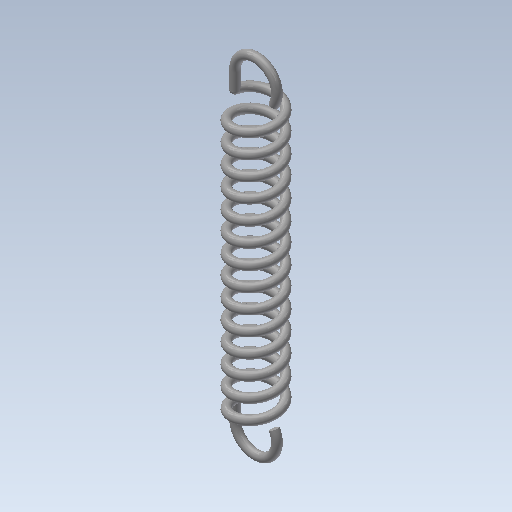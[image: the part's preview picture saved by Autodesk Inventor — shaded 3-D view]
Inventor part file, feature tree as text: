
AUTODESK INVENTOR PART (.ipt)
format: ipt  version: 2020.1 (Build 241239000, 239)  size: 1,151,488 bytes
history: native  units: mm
features: sketch x104, plane x32, other x32, extrude x10, sweep x6
ambient origin geometry x8: Origin, YZ Plane, XZ Plane, XY Plane, X Axis, Y Axis, Z Axis, Center Point
bodies: Solid1 (feature_tree)
feature tree (184):
  sketch  "Sketch1"  dims[d0=0.125mm d1=1.25mm]
  sketch  "3D Sketch2"
  plane  "Work PlaneSweep1"
  other  "First revolution with hook type 0(Right)"
  sketch  "Sketch8"  dims[d17=90.0deg d24=0.0mm d25=1.142857mm]
  plane  "Work PlaneExtrusion7"
  sketch  "Sketch10"  dims[d28=0.0mm d29=90.0deg d30=90.0deg d31=0.0mm d32=0.0mm d33=0.5mm]
  plane  "Work PlaneSweep2"
  sweep  "Sweep2"
  other  "Second revolution with hook type 0(Right)"
  sketch  "Sketch12"  dims[d38=90.0deg d54=10.0mm d55=10.0mm]
  plane  "Work PlaneExtrusion8"
  sketch  "Sketch110"  dims[d367=29.670597mm]
  sketch  "3D Sketch20"
  plane  "Work PlaneSweep3"
  sketch  "3D Sketch3"
  plane  "Work PlaneSweep6"
  other  "First revolution with hook type 0(Left)"
  sketch  "Sketch24"  dims[d180=90.0deg]
  plane  "Work PlaneExtrusion5"
  sketch  "Sketch18"  dims[d169=300.0deg d170=1.0mm]
  plane  "Work PlaneSweep7"
  sweep  "Sweep7"
  other  "Second revolution with hook type 0(Left)"
  sketch  "Sketch20"  dims[d173=300.0deg d174=1.0mm]
  plane  "Work PlaneExtrusion6"
  sketch  "Sketch22"  dims[d177=1.125mm d178=0.0mm]
  plane  "Work PlaneSweep8"
  other  "First revolution with hook type 1(Left)"
  sketch  "Sketch27"  dims[d182=1.125mm]
  plane  "Work PlaneExtrusion9"
  extrude  "Extrusion9"  TaperAngle=90.0deg  [1 undecoded]
  sketch  "Sketch29"  dims[d184=30.0mm d185=30.0mm d186=30.0mm]
  plane  "Work PlaneSweep9"
  other  "Second revolution with hook type 1(Left)"
  sketch  "Sketch32"  dims[d189=1.25mm]
  plane  "Work PlaneExtrusion10"
  sketch  "Sketch34"  dims[d191=300.0deg]
  sketch  "3D Sketch22"
  plane  "Work PlaneSweep10"
  other  "First revolution with hook type 1(Right)"
  sketch  "Sketch42"  dims[d195=40.0mm]
  plane  "Work PlaneExtrusion11"
  extrude  "Extrusion11"  Depth=1.142857mm TaperAngle=0.0deg
  sketch  "Sketch44"  dims[d197=0.0mm]
  plane  "Work PlaneSweep11"
  other  "Second revolution with hook type 1(Right)"
  sketch  "Sketch112"  dims[d373=20.0mm]
  plane  "Work PlaneExtrusion12"
  sketch  "Sketch114"  dims[d375=0.0mm]
  sketch  "3D Sketch24"
  plane  "Work PlaneSweep12"
  sketch  "Sketch46"  dims[d199=300.0deg]
  other  "First sweep with hook type 2(Left)"
  sweep  "SweepLeftHook21"
  sketch  "Sketch48"  dims[d200=1.0mm]
  other  "Second sweep with hook type 2(Left)"
  sweep  "SweepLeftHook22"
  sketch  "Sketch50"  dims[d201=0.0mm]
  other  "First sweep with hook type 2(Right)"
  sweep  "SweepRightHook21"
  sketch  "Sketch52"  dims[d202=90.0deg]
  other  "Second sweep with hook type 2(Right)"
  sweep  "SweepRightHook22"
  other  "First revolution with hook type 3(Left)"
  extrude  "Extrusion1"  Depth=20.0mm
  other  "Second revolution with hook type 3(Left)"
  extrude  "Extrusion2"  Depth=20.0mm
  sketch  "Sketch60"  dims[d209=90.0deg]
  plane  "Work PlaneSweep20"
  other  "First revolution with hook type 3(Right)"
  extrude  "Extrusion3"  Depth=20.0mm
  other  "Second revolution with hook type 3(Right)"
  extrude  "Extrusion4"  Depth=1.0mm
  sketch  "Sketch68"  dims[d216=40.0mm]
  plane  "Work Plane46"
  other  "First revolution with hook type 4(Left)"
  sketch  "Sketch71"  dims[d223=90.0deg]
  plane  "Work PlaneExtrusion13"
  extrude  "Extrusion13"  TaperAngle=90.0deg  [1 undecoded]
  sketch  "Sketch73"  dims[d229=90.0deg]
  plane  "Work PlaneSweep23"
  other  "Second revolution with hook type 4(Left)"
  sketch  "Sketch76"  dims[d238=50.0mm]
  plane  "Work PlaneExtrusion14"
  sketch  "Sketch78"  dims[d243=60.0mm]
  sketch  "3D Sketch26"
  plane  "Work PlaneSweep24"
  other  "First revolution with hook type 4(Right)"
  sketch  "Sketch86"  dims[d269=60.0mm]
  plane  "Work PlaneExtrusion15"
  extrude  "Extrusion15"  Depth=1.0mm
  sketch  "Sketch88"  dims[d282=60.0mm]
  plane  "Work PlaneSweep25"
  other  "Second revolution with hook type 4(Right)"
  sketch  "Sketch116"  dims[d377=210.0deg]
  plane  "Work PlaneExtrusion16"
  sketch  "Sketch118"  dims[d381=20.0mm]
  sketch  "3D Sketch28"
  plane  "Work PlaneSweep26"
  other  "First revolution with hook type 5(Left)"
  sketch  "Sketch91"  dims[d301=10.0mm d302=15.0mm d303=0.0mm d304=90.0deg d305=90.0deg d306=0.0mm d307=0.0mm]
  plane  "Work PlaneExtrusion17"
  extrude  "Extrusion17"  TaperAngle=300.0deg  [1 undecoded]
  other  "Second revolution with hook type 5(Left)"
  sketch  "Sketch95"  dims[d320=1.125mm]
  plane  "Work PlaneExtrusion18"
  other  "First revolution with hook type 5(Right)"
  sketch  "Sketch99"  dims[d331=1.0mm]
  plane  "Work PlaneExtrusion19"
  other  "Second revolution with hook type 5(Right)"
  sketch  "Sketch103"  dims[d364=1.0mm]
  plane  "Work PlaneExtrusion20"
  extrude  "Extrusion20"  TaperAngle=0.0deg  [1 undecoded]
  sketch  "Sketch105"  dims[d366=10.0mm]
  other  "First coil with hook type 6(Left)"
  other  "Second coil with hook type 6(Left)"
  other  "First coil with hook type 6(Right)"
  other  "Second coil with hook type 6(Right)"
  other  "Srf1"
  sketch  "Sketch3"  dims[d2=1.142857mm d3=10.0mm d4=140.0mm]
  sketch  "Sketch4"  dims[d5=0.0mm d6=90.0deg d7=90.0deg d8=0.0mm d9=0.0mm d12=0.5mm]
  sketch  "Sketch7"  dims[d13=0.0mm d14=90.0deg]
  other  "Srf2"
  sketch  "3D Sketch14"
  sketch  "Sketch16"  dims[d149=90.0deg d152=20.0mm]
  sketch  "Sketch26"  dims[d181=300.0deg]
  sketch  "Sketch31"  dims[d188=40.0mm]
  sketch  "Sketch36"  dims[d193=0.0mm]
  sketch  "Sketch41"  dims[d194=90.0deg]
  sketch  "Sketch54"  dims[d203=40.0mm]
  sketch  "Sketch55"  dims[d204=1.25mm d205=0.0mm]
  sketch  "Sketch56"  dims[d206=300.0deg]
  sketch  "Sketch58"  dims[d207=1.0mm]
  sketch  "Sketch59"  dims[d208=0.0mm]
  sketch  "Sketch61"  dims[d210=1.25mm]
  sketch  "Sketch62"  dims[d211=0.0mm]
  sketch  "Sketch63"  dims[d212=90.0deg]
  sketch  "Sketch64"  dims[d213=300.0deg]
  sketch  "Sketch66"  dims[d214=1.0mm]
  sketch  "Sketch67"  dims[d215=0.0mm]
  sketch  "Sketch69"  dims[d217=90.0deg]
  sketch  "Sketch70"  dims[d220=50.0mm]
  sketch  "Sketch75"  dims[d235=90.0deg]
  sketch  "Sketch80"  dims[d256=60.0mm]
  sketch  "Sketch85"  dims[d268=90.0deg]
  sketch  "Sketch90"  dims[d300=1.0mm]
  sketch  "Sketch94"  dims[d311=10.0mm d312=15.0mm d313=0.0mm d314=90.0deg d315=90.0deg d316=0.0mm d317=0.0mm d318=70.0mm d319=70.0mm]
  sketch  "Sketch98"  dims[d330=1.125mm]
  sketch  "Sketch102"  dims[d361=10.0mm]
  sketch  "Sketch13"  dims[d72=0.0mm d73=0.0mm d79=90.0deg]
  sketch  "Sketch111"  dims[d368=0.0mm]
  sketch  "Sketch33"  dims[d190=0.0mm]
  sketch  "Sketch35"  dims[d192=1.0mm]
  sketch  "Sketch113"  dims[d374=1.0mm]
  sketch  "Sketch115"  dims[d376=20.0mm]
  sketch  "Sketch77"  dims[d242=90.0deg]
  sketch  "Sketch79"  dims[d255=90.0deg]
  sketch  "Sketch117"  dims[d378=0.0mm]
  sketch  "Sketch119"  dims[d384=1.0mm d385=0.0mm d386=20.0mm d387=210.0deg d388=0.0mm d391=50.0mm d394=1.0mm d395=0.0mm d396=50.0mm d397=29.670597mm d398=0.0mm d401=50.0mm d404=1.0mm d405=0.0mm d406=50.0mm d407=29.670597mm d408=0.0mm d411=60.0mm d423=60.0mm d433=1.0mm d434=0.0mm d435=1.0mm d436=1.0mm d437=10.0mm d438=15.0mm d439=0.0mm d440=90.0deg d441=90.0deg d442=0.0mm d443=0.0mm d444=60.0mm d447=60.0mm d457=1.0mm d458=0.0mm d459=60.0mm d469=90.0deg d478=90.0deg d479=1.0mm d480=1.0mm d481=25.4mm d482=15.0mm d483=0.0mm d484=90.0deg d485=90.0deg d486=0.0mm d487=0.0mm d491=10.0mm d498=10.0mm d501=0.0mm d502=1.0mm d503=0.0mm d504=210.0deg d505=0.0mm d506=0.0mm d507=1.0mm d508=0.0mm d509=29.670597mm d510=0.0mm d511=10.0mm d512=0.0mm d513=1.0mm d514=0.0mm d515=29.670597mm d516=0.0mm d517=0.0mm d518=1.0mm d519=0.0mm d520=1.0mm d521=1.0mm d522=10.0mm d523=15.0mm d524=0.0mm d525=90.0deg d526=90.0deg d527=0.0mm d528=0.0mm d529=60.0mm d530=50.0mm d531=0.0mm d532=1.0mm d533=0.0mm d534=20.0mm d535=210.0deg d536=0.0mm d537=0.0mm d538=1.0mm d539=0.0mm d540=29.670597mm d541=0.0mm d542=50.0mm d543=0.0mm d544=1.0mm d545=0.0mm d546=60.0mm d547=1.0mm d548=1.0mm d549=10.0mm d550=15.0mm d551=0.0mm d552=90.0deg d553=90.0deg d554=0.0mm d555=0.0mm d561=10.0mm d564=0.0mm d565=1.0mm d566=0.0mm d567=10.0mm d569=29.670597mm d570=0.0mm d571=90.0deg d578=0.0mm d579=0.5mm d580=1.0mm d581=0.0mm d584=10.0mm d585=10.0mm d588=29.670597mm d589=0.0mm d590=0.0mm d591=0.0mm d592=0.0mm d593=0.0mm d594=0.0mm d595=0.0mm d596=0.0mm d597=0.0mm d598=0.0mm d599=0.0mm d600=0.0mm d601=0.0mm d602=0.0mm d603=0.0mm d604=0.0mm d605=0.0mm d606=0.0mm d607=0.0mm d608=0.0mm d609=0.0mm d610=0.0mm d611=0.0mm]
  sketch  "Sketch96"  dims[d321=1.0mm]
  sketch  "Sketch97"  dims[d322=10.0mm d323=15.0mm d324=0.0mm d325=90.0deg d326=90.0deg d327=0.0mm d328=0.0mm d329=70.0mm]
  sketch  "Sketch104"  dims[d365=0.0mm]
  sketch  "Sketch43"  dims[d196=1.25mm]
  sketch  "Sketch45"  dims[d198=90.0deg]
  sketch  "Sketch9"  dims[d26=10.0mm d27=140.0mm]
  sketch  "Sketch11"  dims[d34=0.0mm d36=0.0mm]
  sketch  "Sketch87"  dims[d281=90.0deg]
  sketch  "Sketch89"  dims[d299=1.125mm]
  sketch  "Sketch100"  dims[d332=10.0mm d333=15.0mm d334=0.0mm d335=90.0deg d336=90.0deg d337=0.0mm d338=0.0mm d339=70.0mm]
  sketch  "Sketch101"  dims[d350=10.0mm d352=10.0mm d353=10.0mm d356=10.0mm]
  sketch  "Sketch28"  dims[d183=0.0mm]
  sketch  "Sketch30"  dims[d187=90.0deg]
  sketch  "Sketch72"  dims[d226=50.0mm]
  sketch  "Sketch74"  dims[d232=50.0mm]
  sketch  "Sketch92"  dims[d308=1.125mm]
  sketch  "Sketch93"  dims[d310=1.0mm]
  sketch  "Sketch21"  dims[d175=0.0mm d176=300.0deg]
  sketch  "Sketch23"  dims[d179=30.0mm]
  sketch  "Sketch15"  dims[d86=90.0deg d87=20.0mm d90=20.0mm]
  sketch  "Sketch17"  dims[d155=90.0deg d156=20.0mm]
  sketch  "Sketch19"  dims[d171=0.0mm d172=90.0deg]
  other  "Base Coil(Right)"
  other  "Base Coil(Left)"
note: 4 required parameter values undecoded (feature->parameter linkage not recoverable at this tier; creation-order binding heuristic only, values carry confidence <= 0.55)
